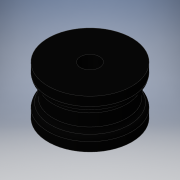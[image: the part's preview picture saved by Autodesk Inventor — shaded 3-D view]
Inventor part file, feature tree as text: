
AUTODESK INVENTOR PART (.ipt)
format: ipt  version: 2016 (Build 200138000, 138)  size: 166,912 bytes
history: native  units: in
note: dims shown in document units (in); Inventor stores cm internally (conversion verified against a paired STEP export)
features: extrude x4, sketch x4, fillet x3
ambient origin geometry x8: Origin, YZ Plane, XZ Plane, XY Plane, X Axis, Y Axis, Z Axis, Center Point
bodies: Solid1 (feature_tree)
feature tree (11):
  extrude  "Extrusion1"  Depth=2.15in TaperAngle=0.0deg
  sketch  "Sketch2"  dims[d3=7.87in d4=7.87in]
  sketch  "Sketch3"  dims[d5=1.2in d6=0.0in d7=1.2in d8=0.0in]
  extrude  "Extrusion2"  Depth=7.87in
  extrude  "Extrusion3"  Depth=1.2in TaperAngle=0.0deg
  extrude  "Extrusion4"  Depth=4.55in TaperAngle=0.0deg
  fillet  "Fillet1"  Radius=0.5in
  fillet  "Fillet2"  Radius=0.5in
  fillet  "Fillet3"  Radius=0.5in
  sketch  "Sketch1"  dims[d0=6.91in d1=2.15in d2=0.0in]
  sketch  "Sketch4"  dims[d9=1.8in d10=4.55in d11=0.0in d12=0.5in d13=0.5in d14=0.5in]
